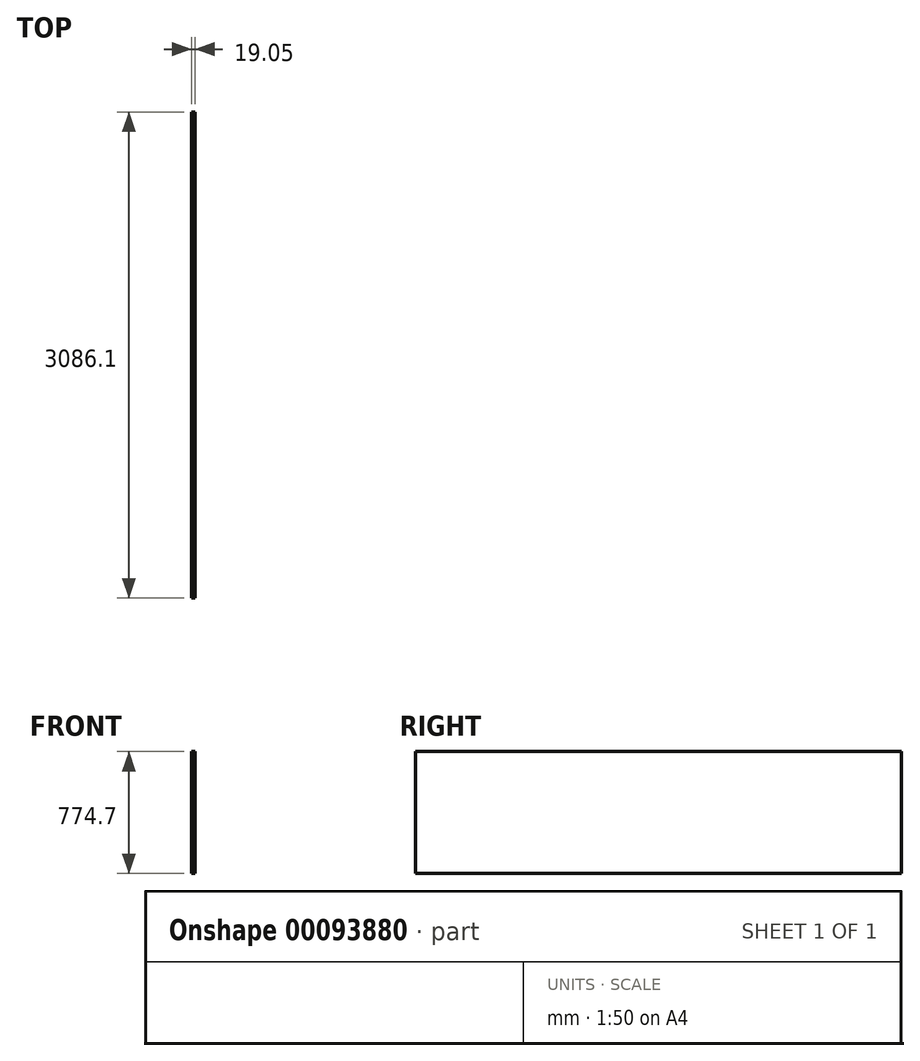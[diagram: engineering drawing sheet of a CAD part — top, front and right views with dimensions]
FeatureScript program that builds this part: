
annotation { "Feature Type Name" : "Feature", "Feature Type Description" : "" }
export const myFeature = defineFeature(function(context is Context, id is Id, definition is map)
    precondition{}
    {
        {
            var Q0;
            Q0=qCreatedBy(makeId("Right.planeOp"),FACE);
            var sketch = newSketch(context, id + "F0", { "sketchPlane" : qUnion([Q0])});
            skLineSegment(sketch, "E0.bottom", {"start": v(-1543.05, 774.7) * mm, "end": v(1543.05, 774.7) * mm});
            skLineSegment(sketch, "E0.top", {"start": v(-1543.05, 0) * mm, "end": v(1543.05, 0) * mm});
            skLineSegment(sketch, "E0.left", {"start": v(-1543.05, 774.7) * mm, "end": v(-1543.05, 0) * mm});
            skLineSegment(sketch, "E0.right", {"start": v(1543.05, 774.7) * mm, "end": v(1543.05, 0) * mm});
            skSolve(sketch);
        }
        {
            var Q0;
            Q0=qSketchRegion(id+"F0",true);
            extrude(context, id + "F1", {"entities" : qUnion([Q0]), "depth" : 19.05 * mm});
        }
    });
